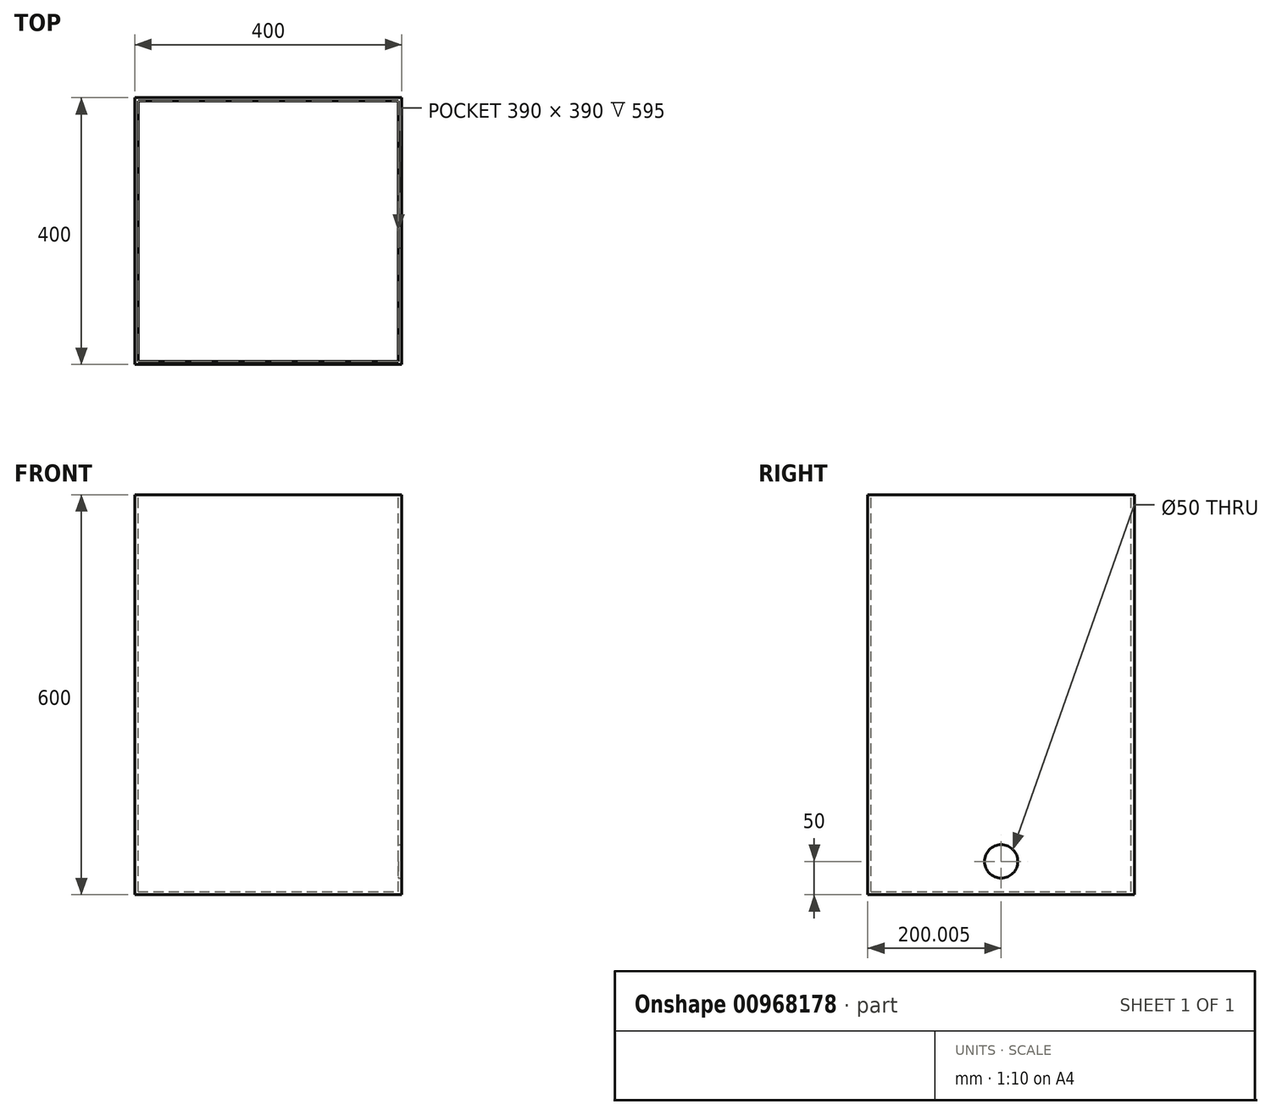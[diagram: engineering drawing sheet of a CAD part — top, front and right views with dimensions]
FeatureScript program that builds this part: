
annotation { "Feature Type Name" : "Feature", "Feature Type Description" : "" }
export const myFeature = defineFeature(function(context is Context, id is Id, definition is map)
    precondition{}
    {
        {
            var Q0;
            Q0=qCreatedBy(makeId("Top.planeOp"),FACE);
            var sketch = newSketch(context, id + "F0", { "sketchPlane" : qUnion([Q0])});
            skLineSegment(sketch, "E0", {"start": v(-132.52, -191.46) * mm, "end": v(-132.52, 208.54) * mm});
            skLineSegment(sketch, "E1", {"start": v(-132.52, 208.54) * mm, "end": v(267.48, 208.54) * mm});
            skLineSegment(sketch, "E2", {"start": v(-132.52, -191.46) * mm, "end": v(267.48, -191.46) * mm});
            skLineSegment(sketch, "E3", {"start": v(267.48, 208.54) * mm, "end": v(267.48, -191.46) * mm});
            skSolve(sketch);
        }
        {
            var Q0;
            Q0=makeQuery(id+"F0.imprint","IMPRINT",FACE,{"disambiguationData":[TD([[makeQuery(id+"F0.imprint","IMPRINT",EDGE,{"derivedFrom":sQuery(id+"F0.wireOp",EDGE,"E0")}),-1.0]])]});
            extrude(context, id + "F1", {"entities" : qUnion([Q0]), "oppositeDirection" : true, "depth" : 600 * mm, "offsetDistance" : 25 * mm});
        }
        {
            var Q0;
            Q0=makeQuery(id+"F1.opExtrude","CAP_FACE",FACE,{"disambiguationData":[OSD([sQuery(id+"F0.wireOp",EDGE,"E0"),sQuery(id+"F0.wireOp",EDGE,"E1"),sQuery(id+"F0.wireOp",EDGE,"E2"),sQuery(id+"F0.wireOp",EDGE,"E3")])],"isStart":true});
            shell(context, id + "F2", {"entities" : qUnion([Q0]), "thickness" : 5 * mm});
        }
        {
            var Q0;
            Q0=makeQuery(id+"F1.opExtrude","SWEPT_FACE",FACE,{"disambiguationData":[OSD([sQuery(id+"F0.wireOp",EDGE,"E3")])]});
            var sketch = newSketch(context, id + "F3", { "sketchPlane" : qUnion([Q0])});
            skCircle(sketch, "E4", {"center": v(8.54, -550) * mm, "radius": 25 * mm});
            skSolve(sketch);
        }
        {
            var Q0;
            Q0 = qSketchRegion(id + "F3", true);
            extrude(context, id + "F4", {"entities" : qUnion([Q0]), "operationType" : NewBodyOperationType.REMOVE, "oppositeDirection" : true, "depth" : 30 * mm, "offsetDistance" : 25 * mm});
        }
    });
